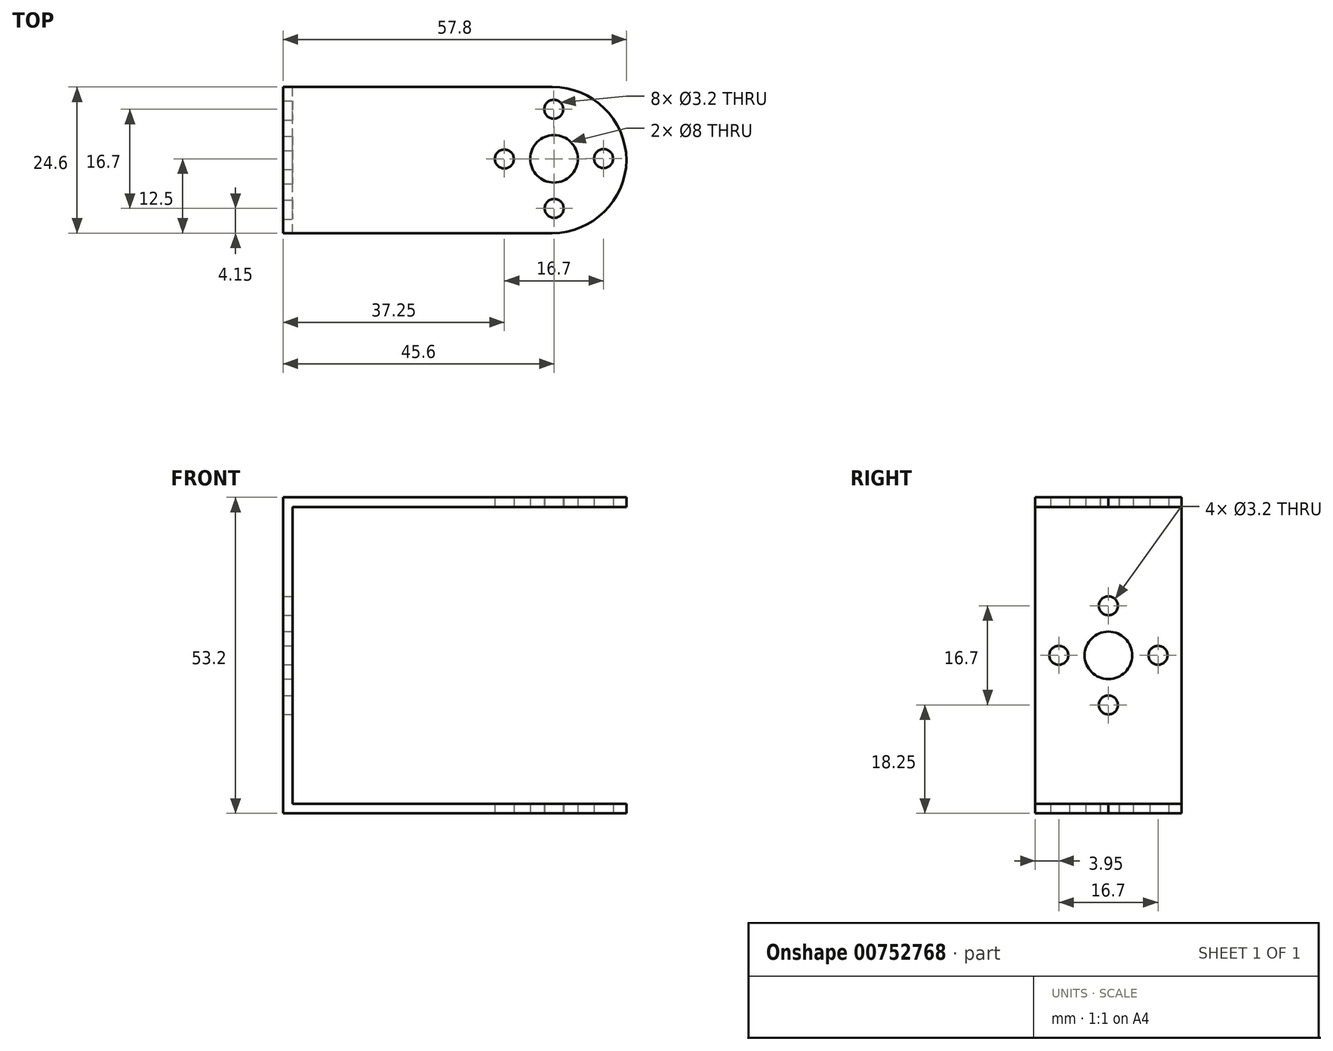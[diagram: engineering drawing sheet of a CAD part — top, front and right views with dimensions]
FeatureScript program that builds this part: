
annotation { "Feature Type Name" : "Feature", "Feature Type Description" : "" }
export const myFeature = defineFeature(function(context is Context, id is Id, definition is map)
    precondition{}
    {
        {
            var Q0;
            Q0=qCreatedBy(makeId("Front.planeOp"),FACE);
            var sketch = newSketch(context, id + "F0", { "sketchPlane" : qUnion([Q0])});
            skLineSegment(sketch, "E0.bottom", {"start": v(28.9, -26.6) * mm, "end": v(-28.9, -26.6) * mm});
            skLineSegment(sketch, "E0.top", {"start": v(28.9, 26.6) * mm, "end": v(-28.9, 26.6) * mm});
            skLineSegment(sketch, "E0.right", {"start": v(-28.9, -26.6) * mm, "end": v(-28.9, 26.6) * mm});
            skPoint(sketch, "E0.middle", {"position": v(0, 0) * mm});
            skLineSegment(sketch, "E1.0", {"start": v(28.9, 25) * mm, "end": v(-27.3, 25) * mm});
            skLineSegment(sketch, "E2.0", {"start": v(28.9, -25) * mm, "end": v(-27.3, -25) * mm});
            skLineSegment(sketch, "E3.0", {"start": v(-27.3, -25) * mm, "end": v(-27.3, 25) * mm});
            skLineSegment(sketch, "E4", {"start": v(28.9, 26.6) * mm, "end": v(28.9, 25) * mm});
            skLineSegment(sketch, "E5", {"start": v(28.9, -26.6) * mm, "end": v(28.9, -25) * mm});
            skSolve(sketch);
        }
        {
            var Q0;
            Q0 = qSketchRegion(id + "F0", true);
            extrude(context, id + "F1", {"entities" : qUnion([Q0]), "depth" : 24.6 * mm, "offsetDistance" : 25 * mm});
        }
        {
            var Q0;
            Q0=makeQuery(id+"F1.opExtrude","CAP_EDGE",EDGE,{"disambiguationData":[OSD([sQuery(id+"F0.wireOp",EDGE,"E5")])],"isStart":false});
            var Q1;
            Q1=makeQuery(id+"F1.opExtrude","CAP_EDGE",EDGE,{"disambiguationData":[OSD([sQuery(id+"F0.wireOp",EDGE,"E5")])],"isStart":true});
            fillet(context, id + "F2", {"entities" : qUnion([Q0, Q1]), "radius" : 12.5 * mm, "tangentPropagation" : true, "allowEdgeOverflow" : false});
        }
        {
            var Q0;
            Q0=makeQuery(id+"F1.opExtrude","CAP_EDGE",EDGE,{"disambiguationData":[OSD([sQuery(id+"F0.wireOp",EDGE,"E4")])],"isStart":false});
            var Q1;
            Q1=makeQuery(id+"F1.opExtrude","CAP_EDGE",EDGE,{"disambiguationData":[OSD([sQuery(id+"F0.wireOp",EDGE,"E4")])],"isStart":true});
            fillet(context, id + "F3", {"entities" : qUnion([Q0, Q1]), "radius" : 12.5 * mm, "tangentPropagation" : true, "allowEdgeOverflow" : false});
        }
        {
            var Q0;
            Q0=makeQuery(id+"F1.opExtrude","SWEPT_FACE",FACE,{"disambiguationData":[OSD([sQuery(id+"F0.wireOp",EDGE,"E0.bottom")])]});
            var sketch = newSketch(context, id + "F4", { "sketchPlane" : qUnion([Q0])});
            skPoint(sketch, "E6.endSnap0", {"position": v(-28.9, 12.3) * mm});
            skCircle(sketch, "E7", {"center": v(16.7, 12.1) * mm, "radius": 4 * mm});
            skCircle(sketch, "E8", {"center": v(16.66, 3.75) * mm, "radius": 1.6 * mm});
            skCircle(sketch, "E9.1.0", {"center": v(8.35, 12.14) * mm, "radius": 1.6 * mm});
            skCircle(sketch, "E9.2.0", {"center": v(16.74, 20.45) * mm, "radius": 1.6 * mm});
            skCircle(sketch, "E10.MirrorC", {"center": v(25.05, 12.06) * mm, "radius": 1.6 * mm});
            skSolve(sketch);
        }
        {
            var Q0;
            Q0 = qSketchRegion(id + "F4", true);
            extrude(context, id + "F5", {"entities" : qUnion([Q0]), "operationType" : NewBodyOperationType.REMOVE, "oppositeDirection" : true, "depth" : 100 * mm, "offsetDistance" : 25 * mm});
        }
        {
            var Q0;
            Q0=makeQuery(id+"F1.opExtrude","SWEPT_FACE",FACE,{"disambiguationData":[OSD([sQuery(id+"F0.wireOp",EDGE,"E3.0")])]});
            var sketch = newSketch(context, id + "F6", { "sketchPlane" : qUnion([Q0])});
            skCircle(sketch, "E11", {"center": v(-12.3, 0) * mm, "radius": 4 * mm});
            skPoint(sketch, "E11.centerSnap0", {"position": v(-12.3, -25) * mm});
            skLineSegment(sketch, "E12", {"start": v(-12.3, 0) * mm, "end": v(-3.95, 0) * mm});
            skCircle(sketch, "E13", {"center": v(-3.95, 0) * mm, "radius": 1.6 * mm});
            skCircle(sketch, "E14.1.0", {"center": v(-12.3, 8.35) * mm, "radius": 1.6 * mm});
            skCircle(sketch, "E14.2.0", {"center": v(-20.65, 0) * mm, "radius": 1.6 * mm});
            skCircle(sketch, "E14.3.0", {"center": v(-12.3, -8.35) * mm, "radius": 1.6 * mm});
            skSolve(sketch);
        }
        {
            var Q0;
            Q0 = qSketchRegion(id + "F6", true);
            extrude(context, id + "F7", {"entities" : qUnion([Q0]), "operationType" : NewBodyOperationType.REMOVE, "oppositeDirection" : true, "depth" : 1.6 * mm, "offsetDistance" : 25 * mm});
        }
    });
